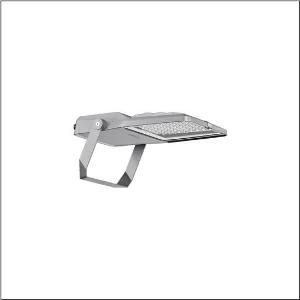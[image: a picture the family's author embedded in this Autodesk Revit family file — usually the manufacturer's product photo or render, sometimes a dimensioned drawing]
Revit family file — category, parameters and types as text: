
# Revit family: floodlight_fl_21_iq_mini___pl52_5xa7772b2d1a_4cc7
name_source: partatom
category: Lighting Fixtures
units: mm (PartAtom-declared; Revit-internal decimal feet)

## family parameters
Cut with Voids When Loaded = No
Host = Face
Light Source = No
Part Type = Normal
Room Calculation Point = No
Round Connector Dimension = Use Diameter
Shared = No

## types (1)
- --- (1 x LED, 6240 lm, 45.5 W, 3000K)
    Apparent Load = 46 VA
    CIE Flux Codes = 26 60 98 100 100
    Color Rendering = 70
    Color Temperature = 3000K
    Default Elevation = 1800 mm
    Description = Floodlight FL 21 iQ mini, floodlight, primary light control with lens, of PMMA, primary optical cover: protective disc, of toughened safety glass, transparent, light distribution: PL52, light emission: direct distribution, installation type: surface-mounted, lamps: LED, High Power LED, rated values: 6.240lm | 45,5W | 137,1lm/W (begin service life); end service life: 6.240lm | 48W; at 50% lumin. flux: 3.120lm | 21,5W | 145,1lm/W, colour temperature: 3000K, colour rendering: CRI > 70, light colour: 730, light setting 1 begin service life: 100% | 6.240lm | 45,5W | 137,1lm/W | 3.000K, light setting 1 end service life: 48W, further light settings possible, control: Street-Remote, Auto-Match, Temp-Guard, Night-Set, Smart-Wire, Desk-Remote (wireless, voltage-free reading and setting of iQ features in the workshop via application-optimized NFC function/RFID function), optimised constant luminous flux control (CLO 2.0), pre-setting: linear dimming characteristic, with terminal, 6-pole, mains connection: 220..240V, AC, 50/60Hz, luminaire housing, of diecast aluminium, powder-coated, SITECO metallic grey (DB 702S), corrosivity category C5 mid according to DIN EN ISO 12944suitable for swimming poolschlorine-resistant, sealing non-destructively replaceable, mounting bracket, of steel, galvanised, powder-coated, SITECO metallic grey (DB 702S), protection rating (complete): IP66, insulation class (complete): insulation class II (safety insulation), certification: CE, ENEC, VDE, protection symbol: D, impact resistance: IK08, permissible operating ambient temperature: -40..+40°C, permissible operating ambient temperature for outdoor applications: -40..+50°C, standard: DIN EN 12944, LABS conformity tested according to VDMA 24364:2018-05, packaging unit: 1 piece

Light Distribution: PL52
    Height = 70 mm
    Lamp = 1 x LED
    Lamp Light Flux = 6240 lm
    Lamp Power = 45.5 W
    Lamp count = 1
    Length = 485 mm
    Luminous efficacy = 137 lm/W
    Manufacturer = Siteco
    ModVariant = No
    Model = 5XA7772B2D1A
    Mounting Place = Pole
    Mounting Type = Pole annexe
    Number of Poles = 1
    OnlyDefault = Yes
    Power Factor = 1
    Product Name = Floodlight FL 21 iQ mini | PL52
    Product group = floodlight | pylon annexe
    ProductGroupID = 6201
    Protection Class = Protection class II
    Protection Degree = IP 66
    RLX_Detail_Level = 1
    RLX_Emergency_Light_Flux = 0 lm
    RLX_Emergency_Type = 0
    RLX_Emergency_Type_DB = No
    RlxData = <blob elided: 96653 chars, md5=469d8475>
    Socket = socket
    Standby Power = 0 W
    System Light Flux = 6240 lm
    System Power = 46 W
    Type Comments = factory setting: luminous flux: 100 % | dim-lin: 254 | 463 mA
    Type Image = l_1006845.jpg
    URL = http://relux.com
    VarID = @adj_165941
    Voltage = 0 V
    Weight = 0.00 kg
    Width = 337 mm

## geometry (parser evidence)
native form markers: Blend x4, Sweep x11
no freeform markers — native parametric forms only
